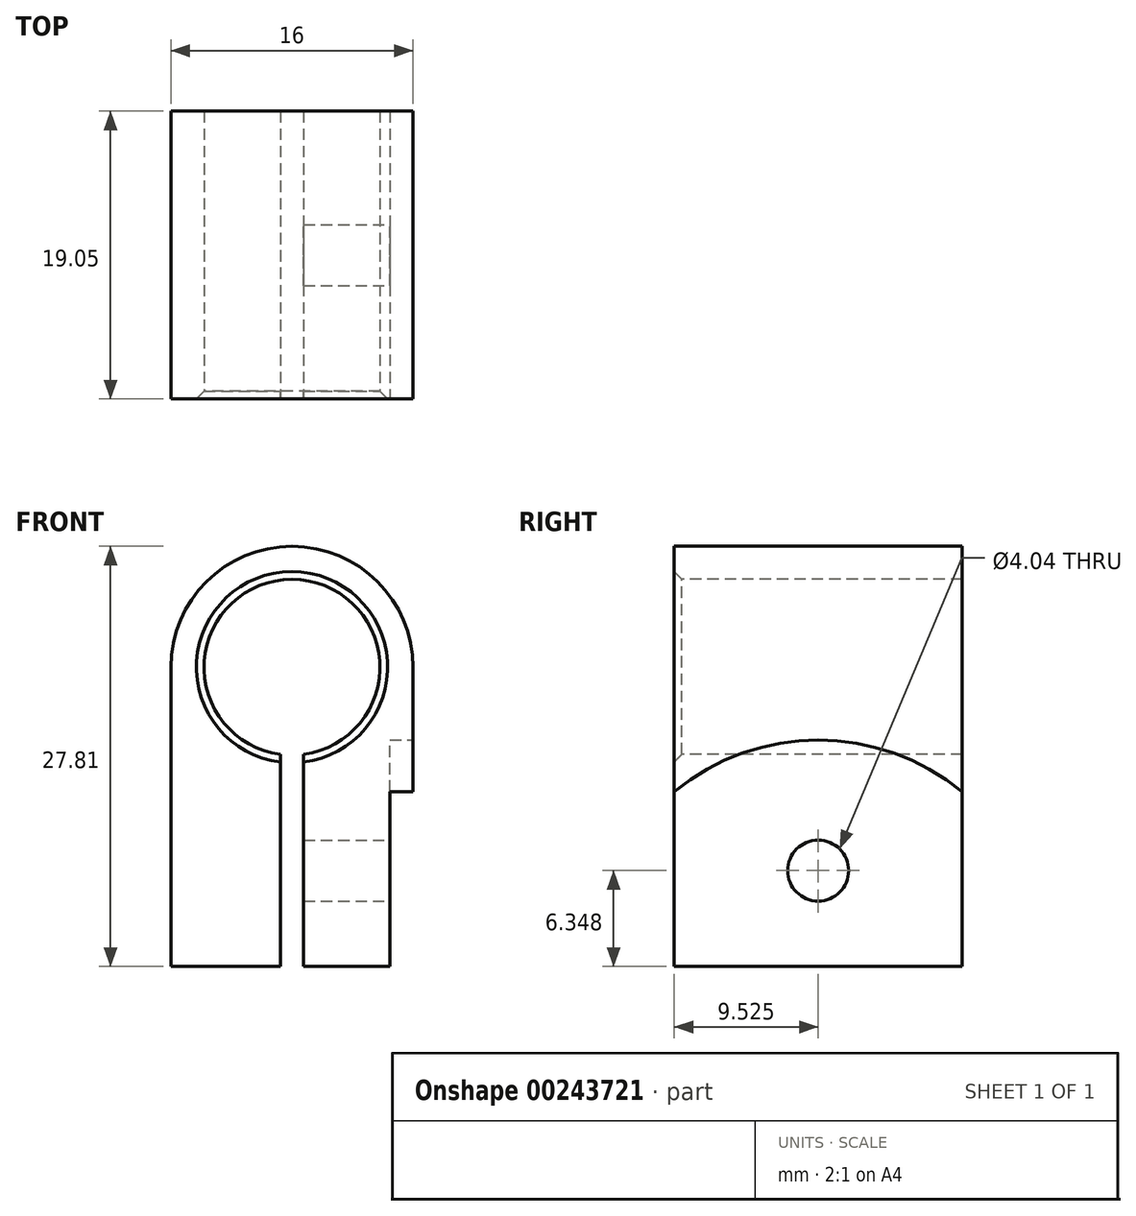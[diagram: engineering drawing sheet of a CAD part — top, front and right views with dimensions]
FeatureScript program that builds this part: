
annotation { "Feature Type Name" : "Feature", "Feature Type Description" : "" }
export const myFeature = defineFeature(function(context is Context, id is Id, definition is map)
    precondition{}
    {
        {
            var Q0;
            Q0=qCreatedBy(makeId("Front.planeOp"),FACE);
            var sketch = newSketch(context, id + "F0", { "sketchPlane" : qUnion([Q0])});
            skArc(sketch, "E0", {"start": v(8, 0) * mm, "mid": v(0, 8) * mm, "end": v(-8, 0) * mm});
            skLineSegment(sketch, "E1", {"start": v(-8, 0) * mm, "end": v(-8, -19.81) * mm});
            skLineSegment(sketch, "E2", {"start": v(-8, -19.81) * mm, "end": v(8, -19.81) * mm});
            skLineSegment(sketch, "E3", {"start": v(8, 0) * mm, "end": v(8, -19.81) * mm});
            skCircle(sketch, "E4", {"center": v(0, 0) * mm, "radius": 5.82 * mm});
            skSolve(sketch);
        }
        {
            var Q0;
            Q0=makeQuery(id+"F0.imprint","IMPRINT",FACE,{"disambiguationData":[TD([[makeQuery(id+"F0.imprint","IMPRINT",EDGE,{"derivedFrom":sQuery(id+"F0.wireOp",EDGE,"E0")}),1.0]])]});
            extrude(context, id + "F1", {"entities" : qUnion([Q0]), "oppositeDirection" : true, "depth" : 19.05 * mm});
        }
        {
            var Q0;
            Q0=makeQuery(id+"F1.opExtrude","CAP_EDGE",EDGE,{"disambiguationData":[OSD([sQuery(id+"F0.wireOp",EDGE,"E4")])],"isStart":true});
            chamfer(context, id + "F2", {"entities" : qUnion([Q0]), "chamferType" : ChamferType.OFFSET_ANGLE, "width" : 0.5 * mm, "oppositeDirection" : false, "angle" : 45 * degree, "tangentPropagation" : true});
        }
        {
            var Q0;
            Q0=makeQuery(id+"F1.opExtrude","CAP_FACE",FACE,{"disambiguationData":[OSD([sQuery(id+"F0.wireOp",EDGE,"E0"),sQuery(id+"F0.wireOp",EDGE,"E1"),sQuery(id+"F0.wireOp",EDGE,"E2"),sQuery(id+"F0.wireOp",EDGE,"E3"),sQuery(id+"F0.wireOp",EDGE,"E4")])],"isStart":true});
            var sketch = newSketch(context, id + "F3", { "sketchPlane" : qUnion([Q0])});
            skLineSegment(sketch, "E5", {"start": v(0, 0) * mm, "end": v(0, -25.98) * mm, "construction": true});
            skLineSegment(sketch, "E6.bottom", {"start": v(-0.76, -19.81) * mm, "end": v(0.76, -19.81) * mm});
            skLineSegment(sketch, "E6.top", {"start": v(-0.76, 0) * mm, "end": v(0.76, 0) * mm});
            skLineSegment(sketch, "E6.left", {"start": v(-0.76, -19.81) * mm, "end": v(-0.76, 0) * mm});
            skLineSegment(sketch, "E6.right", {"start": v(0.76, -19.81) * mm, "end": v(0.76, 0) * mm});
            skSolve(sketch);
        }
        {
            var Q0;
            {var subQ0=sQuery(id+"F3.wireOp",EDGE,"E6.bottom");Q0=makeQuery(id+"F3.imprint","IMPRINT",FACE,{"disambiguationData":[TD([[makeQuery(id+"F3.imprint","IMPRINT",EDGE,{"derivedFrom":subQ0}),1.0]])]});}
            var Q1;
            {var subQ0=sQuery(id+"F3.wireOp",EDGE,"E6.top");Q1=makeQuery(id+"F3.imprint","IMPRINT",FACE,{"disambiguationData":[TD([[makeQuery(id+"F3.imprint","IMPRINT",EDGE,{"derivedFrom":subQ0}),-1.0]])]});}
            extrude(context, id + "F4", {"entities" : qUnion([Q0, Q1]), "operationType" : NewBodyOperationType.REMOVE, "oppositeDirection" : true, "depth" : 25.4 * mm});
        }
        {
            var Q0;
            Q0=makeQuery(id+"F1.opExtrude","SWEPT_FACE",FACE,{"disambiguationData":[OSD([sQuery(id+"F0.wireOp",EDGE,"E3")])]});
            var sketch = newSketch(context, id + "F5", { "sketchPlane" : qUnion([Q0])});
            skLineSegment(sketch, "E7", {"start": v(9.53, -24.7) * mm, "end": v(9.53, -5.31) * mm, "construction": true});
            skCircle(sketch, "E8", {"center": v(9.53, -19.81) * mm, "radius": 14.99 * mm});
            skSolve(sketch);
        }
        {
            var Q0;
            {var subQ1=sQuery(id+"F0.wireOp",EDGE,"E3");var subQ6=makeQuery(id+"F1.opExtrude","SWEPT_EDGE",EDGE,{"disambiguationData":[OSD([sQuery(id+"F0.wireOp",EDGE,"E2"),subQ1])]});Q0=makeQuery(id+"F5.imprint","IMPRINT",FACE,{"disambiguationData":[TD([[makeQuery(id+"F5.imprint","IMPRINT",EDGE,{"derivedFrom":subQ6}),1.0]])]});}
            var Q1;
            {var subQ1=sQuery(id+"F0.wireOp",EDGE,"E3");var subQ6=makeQuery(id+"F1.opExtrude","SWEPT_EDGE",EDGE,{"disambiguationData":[OSD([sQuery(id+"F0.wireOp",EDGE,"E2"),subQ1])]});Q1=makeQuery(id+"F5.imprint","IMPRINT",FACE,{"disambiguationData":[TD([[makeQuery(id+"F5.imprint","IMPRINT",EDGE,{"derivedFrom":subQ6}),-1.0]])]});}
            extrude(context, id + "F6", {"entities" : qUnion([Q0, Q1]), "operationType" : NewBodyOperationType.REMOVE, "oppositeDirection" : true, "depth" : 1.52 * mm});
        }
        {
            var Q0;
            Q0=makeQuery(id+"F6.boolean.opBoolean","COPY",FACE,{"derivedFrom":makeQuery(id+"F6.opExtrude","CAP_FACE",FACE,{"disambiguationData":[OSD([sQuery(id+"F5.wireOp",EDGE,"E8")])],"isStart":false})});
            var sketch = newSketch(context, id + "F7", { "sketchPlane" : qUnion([Q0])});
            skPoint(sketch, "E9", {"position": v(9.53, -13.46) * mm});
            skSolve(sketch);
        }
        {
            var Q0;
            Q0=sQuery(id+"F7.wireOp",VERTEX,"E9");
            var Q1;
            Q1=makeQuery(id+"F1.opExtrude","SWEPT_BODY",BODY,{"disambiguationData":[OSD([sQuery(id+"F0.wireOp",EDGE,"E0"),sQuery(id+"F0.wireOp",EDGE,"E1"),sQuery(id+"F0.wireOp",EDGE,"E2"),sQuery(id+"F0.wireOp",EDGE,"E3"),sQuery(id+"F0.wireOp",EDGE,"E4")])]});
            hole(context, id + "F8", {"style" : HoleStyle.SIMPLE, "endStyle" : HoleEndStyle.BLIND, "standardTappedOrClearance" : lookupTablePath({ "standard" : "ANSI", "engagement" : "75%", "pitch" : "32 tpi", "size" : "#10", "type" : "Tapped" }), "standardBlindInLast" : lookupTablePath({ "standard" : "ANSI", "engagement" : "75%", "pitch" : "32 tpi", "size" : "#10", "type" : "Tapped" }), "holeDiameter" : 4.04 * mm, "holeDepth" : 5.7 * mm, "locations" : qUnion([Q0]), "scope" : qUnion([Q1]), "majorDiameter" : 4.83 * mm});
        }
    });
